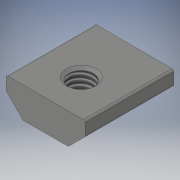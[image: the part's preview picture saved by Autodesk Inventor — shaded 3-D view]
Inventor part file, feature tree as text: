
AUTODESK INVENTOR PART (.ipt)
format: ipt  version: 2019 (Build 230136000, 136)  size: 138,752 bytes
history: native  units: mm
features: other x7, sketch x2, extrude x1, revolve x1, thread x1
ambient origin geometry x8: Origin, YZ Plane, XZ Plane, XY Plane, X Axis, Y Axis, Z Axis, Center Point
bodies: Solid1 (feature_tree)
feature tree (12):
  extrude  "Extrusion1"  TaperAngle=360.0deg  [1 undecoded]
  revolve  "Revolution1"  [1 undecoded]
  thread  "Thread1"  [1 undecoded]
  other  "tnut_XY"
  other  "tnut_YZ"
  other  "tnut_ZX"
  other  "tnut_X"
  other  "tnut_Y"
  other  "tnut_Z"
  other  "tnut_Center"
  sketch  "Sketch_1"  dims[d0=17.78mm d1=0.0mm d2=360.0deg]
  sketch  "Sketch_4"  dims[d3=5.0765mm d4=0.0mm d5=0.0mm]
note: 3 required parameter values undecoded (feature->parameter linkage not recoverable at this tier; creation-order binding heuristic only, values carry confidence <= 0.55)